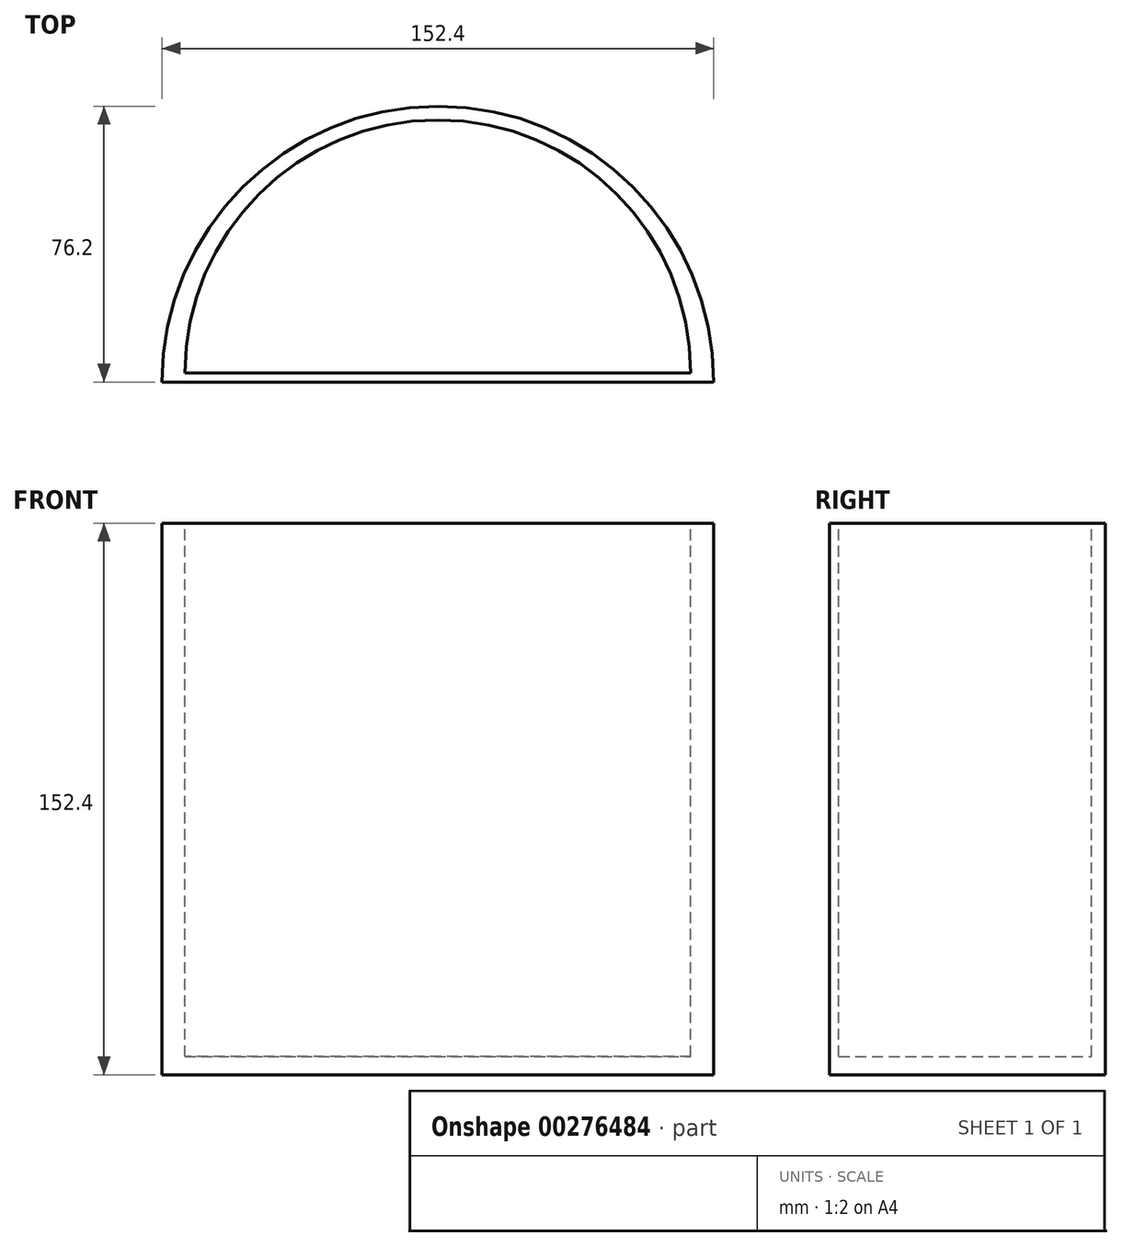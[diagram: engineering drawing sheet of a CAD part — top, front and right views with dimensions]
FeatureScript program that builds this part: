
annotation { "Feature Type Name" : "Feature", "Feature Type Description" : "" }
export const myFeature = defineFeature(function(context is Context, id is Id, definition is map)
    precondition{}
    {
        {
            var Q0;
            Q0=qCreatedBy(makeId("Top.planeOp"),FACE);
            var sketch = newSketch(context, id + "F0", { "sketchPlane" : qUnion([Q0])});
            skArc(sketch, "E0", {"start": v(76.2, 0) * mm, "mid": v(0, 76.2) * mm, "end": v(-76.2, 0) * mm});
            skLineSegment(sketch, "E1", {"start": v(-76.2, 0) * mm, "end": v(76.2, 0) * mm});
            skSolve(sketch);
        }
        {
            var Q0;
            Q0 = qSketchRegion(id + "F0", true);
            extrude(context, id + "F1", {"entities" : qUnion([Q0]), "depth" : 152.4 * mm});
        }
        {
            var Q0;
            Q0=makeQuery(id+"F1.opExtrude","CAP_FACE",FACE,{"disambiguationData":[OSD([sQuery(id+"F0.wireOp",EDGE,"E0"),sQuery(id+"F0.wireOp",EDGE,"E1")])],"isStart":false});
            var sketch = newSketch(context, id + "F2", { "sketchPlane" : qUnion([Q0])});
            skLineSegment(sketch, "E2", {"start": v(0, 0) * mm, "end": v(0, 2.54) * mm});
            skArc(sketch, "E3", {"start": v(69.85, 2.54) * mm, "mid": v(0, 72.4) * mm, "end": v(-69.85, 2.54) * mm});
            skLineSegment(sketch, "E4", {"start": v(0, 2.54) * mm, "end": v(-69.85, 2.54) * mm});
            skLineSegment(sketch, "E5", {"start": v(-69.85, 2.54) * mm, "end": v(69.85, 2.54) * mm});
            skSolve(sketch);
        }
        {
            var Q0;
            Q0 = qSketchRegion(id + "F2", true);
            extrude(context, id + "F3", {"entities" : qUnion([Q0]), "operationType" : NewBodyOperationType.REMOVE, "oppositeDirection" : true, "depth" : 147.32 * mm});
        }
    });
